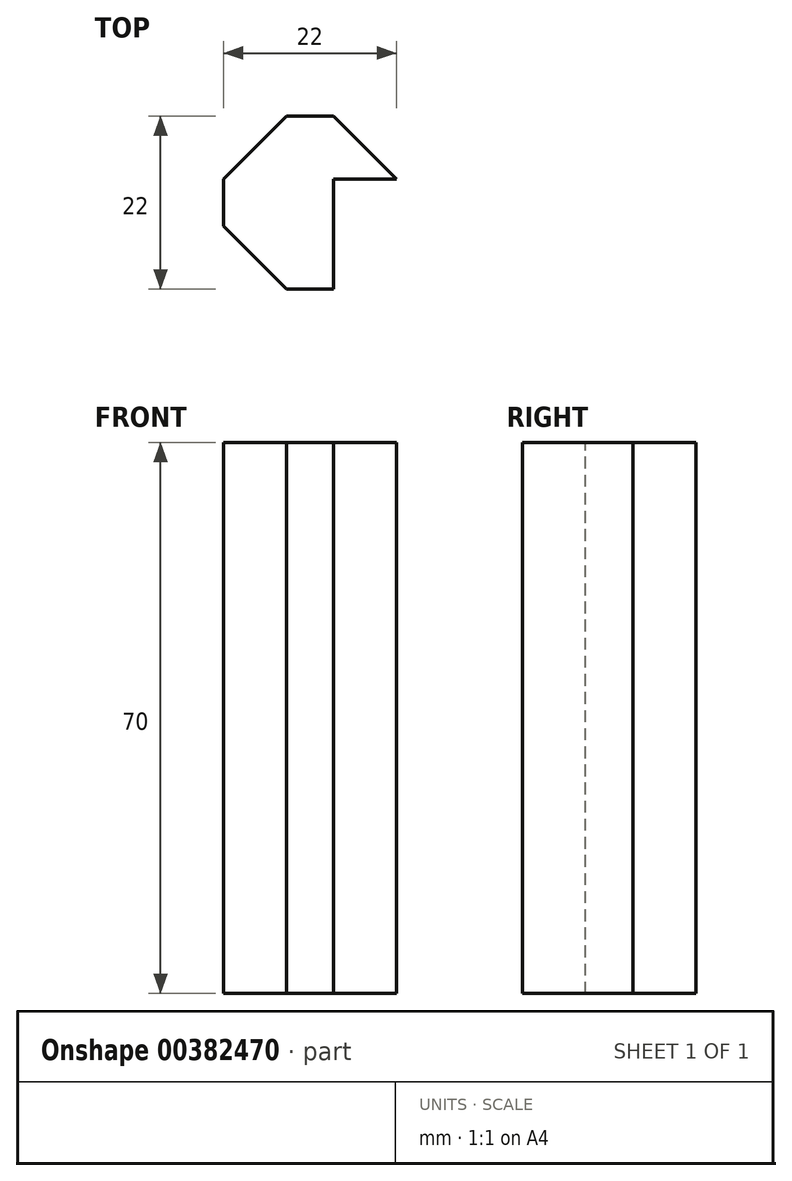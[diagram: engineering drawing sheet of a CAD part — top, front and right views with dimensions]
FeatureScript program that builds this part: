
annotation { "Feature Type Name" : "Feature", "Feature Type Description" : "" }
export const myFeature = defineFeature(function(context is Context, id is Id, definition is map)
    precondition{}
    {
        {
            var Q0;
            Q0=qCreatedBy(makeId("Top.planeOp"),FACE);
            var sketch = newSketch(context, id + "F0", { "sketchPlane" : qUnion([Q0])});
            skLineSegment(sketch, "E0.bottom", {"start": v(7, -11) * mm, "end": v(-7, -11) * mm});
            skLineSegment(sketch, "E0.top", {"start": v(7, 11) * mm, "end": v(-7, 11) * mm});
            skLineSegment(sketch, "E0.left", {"start": v(7, -11) * mm, "end": v(7, 3) * mm});
            skLineSegment(sketch, "E0.right", {"start": v(-7, -11) * mm, "end": v(-7, 11) * mm});
            skPoint(sketch, "E0.middle", {"position": v(0, 0) * mm});
            skLineSegment(sketch, "E1", {"start": v(-7, 11) * mm, "end": v(15, 11) * mm});
            skPoint(sketch, "E1.endSnap0", {"position": v(0, 11) * mm});
            skLineSegment(sketch, "E2", {"start": v(15, 11) * mm, "end": v(15, 3) * mm});
            skLineSegment(sketch, "E3", {"start": v(15, 3) * mm, "end": v(7, 3) * mm});
            skSolve(sketch);
        }
        {
            var Q0;
            Q0 = qSketchRegion(id + "F0", true);
            extrude(context, id + "F1", {"entities" : qUnion([Q0]), "depth" : 70 * mm});
        }
        {
            var Q0;
            Q0=makeQuery(id+"F1.opExtrude","SWEPT_EDGE",EDGE,{"disambiguationData":[OSD([sQuery(id+"F0.wireOp",EDGE,"E0.right"),sQuery(id+"F0.wireOp",EDGE,"E1")])]});
            chamfer(context, id + "F2", {"entities" : qUnion([Q0]), "width" : 8 * mm, "tangentPropagation" : true});
        }
    });
